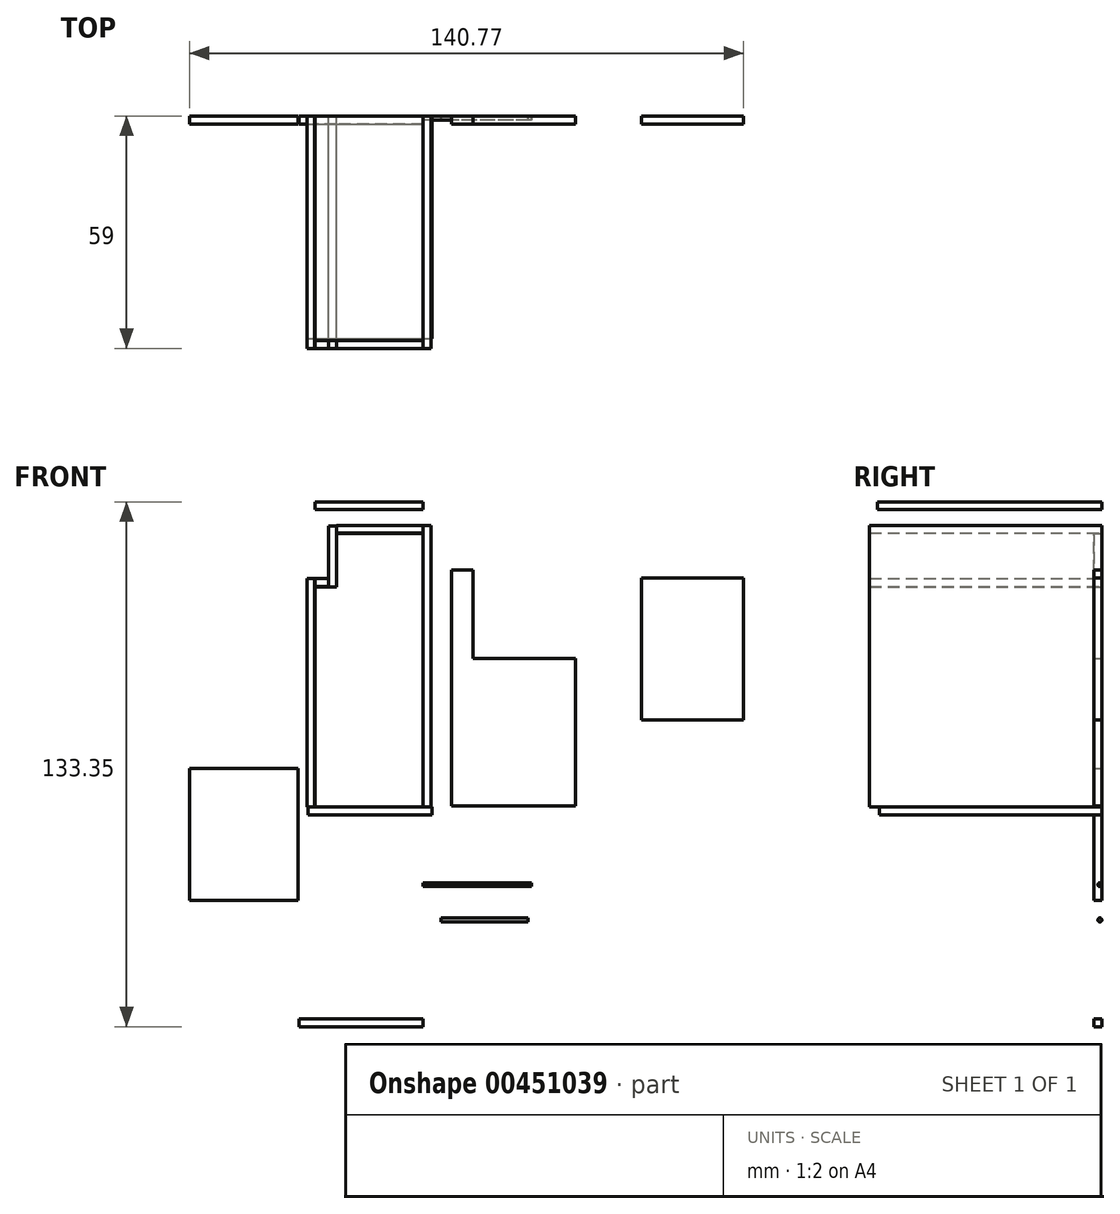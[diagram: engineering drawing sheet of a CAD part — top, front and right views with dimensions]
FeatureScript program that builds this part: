
annotation { "Feature Type Name" : "Feature", "Feature Type Description" : "" }
export const myFeature = defineFeature(function(context is Context, id is Id, definition is map)
    precondition{}
    {
        {
            var Q0;
            Q0=qCreatedBy(makeId("Front.planeOp"),FACE);
            var sketch = newSketch(context, id + "F0", { "sketchPlane" : qUnion([Q0])});
            skLineSegment(sketch, "E0", {"start": v(-27.5, 43.05) * mm, "end": v(-27.5, -12.95) * mm});
            skLineSegment(sketch, "E1", {"start": v(-27.5, -12.95) * mm, "end": v(0, -12.95) * mm});
            skLineSegment(sketch, "E2", {"start": v(0, -12.95) * mm, "end": v(0, 56.55) * mm});
            skLineSegment(sketch, "E3", {"start": v(0, 56.55) * mm, "end": v(-22, 56.55) * mm});
            skLineSegment(sketch, "E4", {"start": v(-22, 56.55) * mm, "end": v(-22, 43.05) * mm});
            skLineSegment(sketch, "E5", {"start": v(-22, 43.05) * mm, "end": v(-27.5, 43.05) * mm});
            skSolve(sketch);
        }
        {
            var Q0;
            Q0=makeQuery(id+"F0.imprint","IMPRINT",FACE,{"disambiguationData":[TD([[makeQuery(id+"F0.imprint","IMPRINT",EDGE,{"derivedFrom":sQuery(id+"F0.wireOp",EDGE,"E0")}),1.0]])]});
            extrude(context, id + "F1", {"entities" : qUnion([Q0]), "depth" : 2 * mm});
        }
        {
            var Q0;
            Q0=qCreatedBy(makeId("Front.planeOp"),FACE);
            var sketch = newSketch(context, id + "F2", { "sketchPlane" : qUnion([Q0])});
            skLineSegment(sketch, "E6.bottom", {"start": v(-24.02, 58.48) * mm, "end": v(-22.02, 58.48) * mm});
            skLineSegment(sketch, "E6.top", {"start": v(-24.02, 42.98) * mm, "end": v(-22.02, 42.98) * mm});
            skLineSegment(sketch, "E6.left", {"start": v(-24.02, 58.48) * mm, "end": v(-24.02, 42.98) * mm});
            skLineSegment(sketch, "E6.right", {"start": v(-22.02, 58.48) * mm, "end": v(-22.02, 42.98) * mm});
            skSolve(sketch);
        }
        {
            var Q0;
            Q0 = qSketchRegion(id + "F2", true);
            extrude(context, id + "F3", {"entities" : qUnion([Q0]), "depth" : 59 * mm});
        }
        {
            var Q0;
            Q0=qCreatedBy(makeId("Front.planeOp"),FACE);
            var sketch = newSketch(context, id + "F4", { "sketchPlane" : qUnion([Q0])});
            skLineSegment(sketch, "E7.bottom", {"start": v(-27.5, 45.1) * mm, "end": v(-24, 45.1) * mm});
            skLineSegment(sketch, "E7.top", {"start": v(-27.5, 43.1) * mm, "end": v(-24, 43.1) * mm});
            skLineSegment(sketch, "E7.left", {"start": v(-27.5, 45.1) * mm, "end": v(-27.5, 43.1) * mm});
            skLineSegment(sketch, "E7.right", {"start": v(-24, 45.1) * mm, "end": v(-24, 43.1) * mm});
            skSolve(sketch);
        }
        {
            var Q0;
            Q0 = qSketchRegion(id + "F4", true);
            extrude(context, id + "F5", {"entities" : qUnion([Q0]), "depth" : 59 * mm});
        }
        {
            var Q0;
            Q0=qCreatedBy(makeId("Front.planeOp"),FACE);
            var sketch = newSketch(context, id + "F6", { "sketchPlane" : qUnion([Q0])});
            skLineSegment(sketch, "E8.bottom", {"start": v(0, 58.58) * mm, "end": v(2, 58.58) * mm});
            skLineSegment(sketch, "E8.top", {"start": v(0, -12.92) * mm, "end": v(2, -12.92) * mm});
            skLineSegment(sketch, "E8.left", {"start": v(0, 58.58) * mm, "end": v(0, -12.92) * mm});
            skLineSegment(sketch, "E8.right", {"start": v(2, 58.58) * mm, "end": v(2, -12.92) * mm});
            skSolve(sketch);
        }
        {
            var Q0;
            Q0 = qSketchRegion(id + "F6", true);
            extrude(context, id + "F7", {"entities" : qUnion([Q0]), "depth" : 59 * mm});
        }
        {
            var Q0;
            Q0=qCreatedBy(makeId("Front.planeOp"),FACE);
            var sketch = newSketch(context, id + "F8", { "sketchPlane" : qUnion([Q0])});
            skLineSegment(sketch, "E9.bottom", {"start": v(-29.53, 45.11) * mm, "end": v(-27.53, 45.11) * mm});
            skLineSegment(sketch, "E9.top", {"start": v(-29.53, -12.89) * mm, "end": v(-27.53, -12.89) * mm});
            skLineSegment(sketch, "E9.left", {"start": v(-29.53, 45.11) * mm, "end": v(-29.53, -12.89) * mm});
            skLineSegment(sketch, "E9.right", {"start": v(-27.53, 45.11) * mm, "end": v(-27.53, -12.89) * mm});
            skSolve(sketch);
        }
        {
            var Q0;
            Q0 = qSketchRegion(id + "F8", true);
            extrude(context, id + "F9", {"entities" : qUnion([Q0]), "operationType" : NewBodyOperationType.ADD, "depth" : 59 * mm});
        }
        {
            var Q0;
            Q0=qCreatedBy(makeId("Front.planeOp"),FACE);
            var sketch = newSketch(context, id + "F10", { "sketchPlane" : qUnion([Q0])});
            skLineSegment(sketch, "E10.bottom", {"start": v(-22, 58.66) * mm, "end": v(0, 58.66) * mm});
            skLineSegment(sketch, "E10.top", {"start": v(-22, 56.66) * mm, "end": v(0, 56.66) * mm});
            skLineSegment(sketch, "E10.left", {"start": v(-22, 58.66) * mm, "end": v(-22, 56.66) * mm});
            skLineSegment(sketch, "E10.right", {"start": v(0, 58.66) * mm, "end": v(0, 56.66) * mm});
            skSolve(sketch);
        }
        {
            var Q0;
            Q0 = qSketchRegion(id + "F10", true);
            extrude(context, id + "F11", {"entities" : qUnion([Q0]), "depth" : 59 * mm});
        }
        {
            var Q0;
            Q0=qCreatedBy(makeId("Front.planeOp"),FACE);
            var sketch = newSketch(context, id + "F12", { "sketchPlane" : qUnion([Q0])});
            skLineSegment(sketch, "E11.bottom", {"start": v(-29.23, -12.89) * mm, "end": v(2.27, -12.89) * mm});
            skLineSegment(sketch, "E11.top", {"start": v(-29.23, -14.89) * mm, "end": v(2.27, -14.89) * mm});
            skLineSegment(sketch, "E11.left", {"start": v(-29.23, -12.89) * mm, "end": v(-29.23, -14.89) * mm});
            skLineSegment(sketch, "E11.right", {"start": v(2.27, -12.89) * mm, "end": v(2.27, -14.89) * mm});
            skSolve(sketch);
        }
        {
            var Q0;
            Q0 = qSketchRegion(id + "F12", true);
            extrude(context, id + "F13", {"entities" : qUnion([Q0]), "depth" : 56.5 * mm});
        }
        {
            var Q0;
            Q0=qCreatedBy(makeId("Front.planeOp"),FACE);
            var sketch = newSketch(context, id + "F14", { "sketchPlane" : qUnion([Q0])});
            skLineSegment(sketch, "E12.bottom", {"start": v(-27.5, 64.64) * mm, "end": v(0, 64.64) * mm});
            skLineSegment(sketch, "E12.top", {"start": v(-27.5, 62.64) * mm, "end": v(0, 62.64) * mm});
            skLineSegment(sketch, "E12.left", {"start": v(-27.5, 64.64) * mm, "end": v(-27.5, 62.64) * mm});
            skLineSegment(sketch, "E12.right", {"start": v(0, 64.64) * mm, "end": v(0, 62.64) * mm});
            skSolve(sketch);
        }
        {
            var Q0;
            Q0 = qSketchRegion(id + "F14", true);
            extrude(context, id + "F15", {"entities" : qUnion([Q0]), "depth" : 57 * mm});
        }
        {
            var Q0;
            Q0=qCreatedBy(makeId("Front.planeOp"),FACE);
            var sketch = newSketch(context, id + "F16", { "sketchPlane" : qUnion([Q0])});
            skLineSegment(sketch, "E13.top", {"start": v(7.18, -12.66) * mm, "end": v(38.68, -12.66) * mm});
            skLineSegment(sketch, "E13.left", {"start": v(7.18, 24.84) * mm, "end": v(7.18, -12.66) * mm});
            skLineSegment(sketch, "E13.right", {"start": v(38.68, 24.84) * mm, "end": v(38.68, -12.66) * mm});
            skLineSegment(sketch, "E14", {"start": v(7.18, 24.84) * mm, "end": v(7.18, 47.34) * mm});
            skLineSegment(sketch, "E15", {"start": v(7.18, 47.34) * mm, "end": v(12.68, 47.34) * mm});
            skLineSegment(sketch, "E16", {"start": v(12.68, 47.34) * mm, "end": v(12.68, 24.84) * mm});
            skLineSegment(sketch, "E17", {"start": v(12.68, 24.84) * mm, "end": v(38.68, 24.84) * mm});
            skSolve(sketch);
        }
        {
            var Q0;
            Q0 = qSketchRegion(id + "F16", true);
            extrude(context, id + "F17", {"entities" : qUnion([Q0]), "depth" : 2 * mm});
        }
        {
            var Q0;
            Q0=qCreatedBy(makeId("Front.planeOp"),FACE);
            var sketch = newSketch(context, id + "F18", { "sketchPlane" : qUnion([Q0])});
            skLineSegment(sketch, "E18.bottom", {"start": v(-59.34, -3.1) * mm, "end": v(-31.84, -3.1) * mm});
            skLineSegment(sketch, "E18.top", {"start": v(-59.34, -36.6) * mm, "end": v(-31.84, -36.6) * mm});
            skLineSegment(sketch, "E18.left", {"start": v(-59.34, -3.1) * mm, "end": v(-59.34, -36.6) * mm});
            skLineSegment(sketch, "E18.right", {"start": v(-31.84, -3.1) * mm, "end": v(-31.84, -36.6) * mm});
            skSolve(sketch);
        }
        {
            var Q0;
            Q0 = qSketchRegion(id + "F18", true);
            extrude(context, id + "F19", {"entities" : qUnion([Q0]), "depth" : 2 * mm});
        }
        {
            var Q0;
            Q0=qCreatedBy(makeId("Front.planeOp"),FACE);
            var sketch = newSketch(context, id + "F20", { "sketchPlane" : qUnion([Q0])});
            skLineSegment(sketch, "E19.bottom", {"start": v(55.43, 45.28) * mm, "end": v(81.43, 45.28) * mm});
            skLineSegment(sketch, "E19.top", {"start": v(55.43, 9.28) * mm, "end": v(81.43, 9.28) * mm});
            skLineSegment(sketch, "E19.left", {"start": v(55.43, 45.28) * mm, "end": v(55.43, 9.28) * mm});
            skLineSegment(sketch, "E19.right", {"start": v(81.43, 45.28) * mm, "end": v(81.43, 9.28) * mm});
            skSolve(sketch);
        }
        {
            var Q0;
            Q0 = qSketchRegion(id + "F20", true);
            extrude(context, id + "F21", {"entities" : qUnion([Q0]), "depth" : 2 * mm});
        }
        {
            var Q0;
            Q0=qCreatedBy(makeId("Front.planeOp"),FACE);
            var sketch = newSketch(context, id + "F22", { "sketchPlane" : qUnion([Q0])});
            skLineSegment(sketch, "E20.bottom", {"start": v(0, -32.13) * mm, "end": v(27.5, -32.13) * mm});
            skLineSegment(sketch, "E20.top", {"start": v(0, -33.13) * mm, "end": v(27.5, -33.13) * mm});
            skLineSegment(sketch, "E20.left", {"start": v(0, -32.13) * mm, "end": v(0, -33.13) * mm});
            skLineSegment(sketch, "E20.right", {"start": v(27.5, -32.13) * mm, "end": v(27.5, -33.13) * mm});
            skSolve(sketch);
        }
        {
            var Q0;
            Q0 = qSketchRegion(id + "F22", true);
            extrude(context, id + "F23", {"entities" : qUnion([Q0]), "depth" : 1 * mm});
        }
        {
            var Q0;
            Q0=makeQuery(id+"F23.opExtrude","CAP_EDGE",EDGE,{"disambiguationData":[OSD([sQuery(id+"F22.wireOp",EDGE,"E20.top")])],"isStart":false});
            var Q1;
            Q1=makeQuery(id+"F23.opExtrude","CAP_EDGE",EDGE,{"disambiguationData":[OSD([sQuery(id+"F22.wireOp",EDGE,"E20.bottom")])],"isStart":false});
            var Q2;
            Q2=makeQuery(id+"F23.opExtrude","CAP_EDGE",EDGE,{"disambiguationData":[OSD([sQuery(id+"F22.wireOp",EDGE,"E20.top")])],"isStart":true});
            var Q3;
            Q3=makeQuery(id+"F23.opExtrude","CAP_EDGE",EDGE,{"disambiguationData":[OSD([sQuery(id+"F22.wireOp",EDGE,"E20.bottom")])],"isStart":true});
            fillet(context, id + "F24", {"entities" : qUnion([Q0, Q1, Q2, Q3]), "radius" : 0.5 * mm, "tangentPropagation" : true, "allowEdgeOverflow" : false});
        }
        {
            var Q0;
            Q0=qCreatedBy(makeId("Front.planeOp"),FACE);
            var sketch = newSketch(context, id + "F25", { "sketchPlane" : qUnion([Q0])});
            skLineSegment(sketch, "E21.bottom", {"start": v(4.58, -41.1) * mm, "end": v(26.58, -41.1) * mm});
            skLineSegment(sketch, "E21.top", {"start": v(4.58, -42.1) * mm, "end": v(26.58, -42.1) * mm});
            skLineSegment(sketch, "E21.left", {"start": v(4.58, -41.1) * mm, "end": v(4.58, -42.1) * mm});
            skLineSegment(sketch, "E21.right", {"start": v(26.58, -41.1) * mm, "end": v(26.58, -42.1) * mm});
            skSolve(sketch);
        }
        {
            var Q0;
            Q0 = qSketchRegion(id + "F25", true);
            extrude(context, id + "F26", {"entities" : qUnion([Q0]), "depth" : 1 * mm});
        }
        {
            var Q0;
            Q0=makeQuery(id+"F26.opExtrude","CAP_EDGE",EDGE,{"disambiguationData":[OSD([sQuery(id+"F25.wireOp",EDGE,"E21.bottom")])],"isStart":false});
            var Q1;
            Q1=makeQuery(id+"F26.opExtrude","CAP_EDGE",EDGE,{"disambiguationData":[OSD([sQuery(id+"F25.wireOp",EDGE,"E21.top")])],"isStart":false});
            var Q2;
            Q2=makeQuery(id+"F26.opExtrude","CAP_EDGE",EDGE,{"disambiguationData":[OSD([sQuery(id+"F25.wireOp",EDGE,"E21.top")])],"isStart":true});
            var Q3;
            Q3=makeQuery(id+"F26.opExtrude","CAP_EDGE",EDGE,{"disambiguationData":[OSD([sQuery(id+"F25.wireOp",EDGE,"E21.bottom")])],"isStart":true});
            fillet(context, id + "F27", {"entities" : qUnion([Q0, Q1, Q2, Q3]), "radius" : 0.5 * mm, "tangentPropagation" : true, "allowEdgeOverflow" : false});
        }
        {
            var Q0;
            Q0=qCreatedBy(makeId("Front.planeOp"),FACE);
            var sketch = newSketch(context, id + "F28", { "sketchPlane" : qUnion([Q0])});
            skLineSegment(sketch, "E22.bottom", {"start": v(-31.5, -66.7) * mm, "end": v(0, -66.7) * mm});
            skLineSegment(sketch, "E22.top", {"start": v(-31.5, -68.7) * mm, "end": v(0, -68.7) * mm});
            skLineSegment(sketch, "E22.left", {"start": v(-31.5, -66.7) * mm, "end": v(-31.5, -68.7) * mm});
            skLineSegment(sketch, "E22.right", {"start": v(0, -66.7) * mm, "end": v(0, -68.7) * mm});
            skSolve(sketch);
        }
        {
            var Q0;
            Q0 = qSketchRegion(id + "F28", true);
            extrude(context, id + "F29", {"entities" : qUnion([Q0]), "depth" : 2 * mm});
        }
    });
